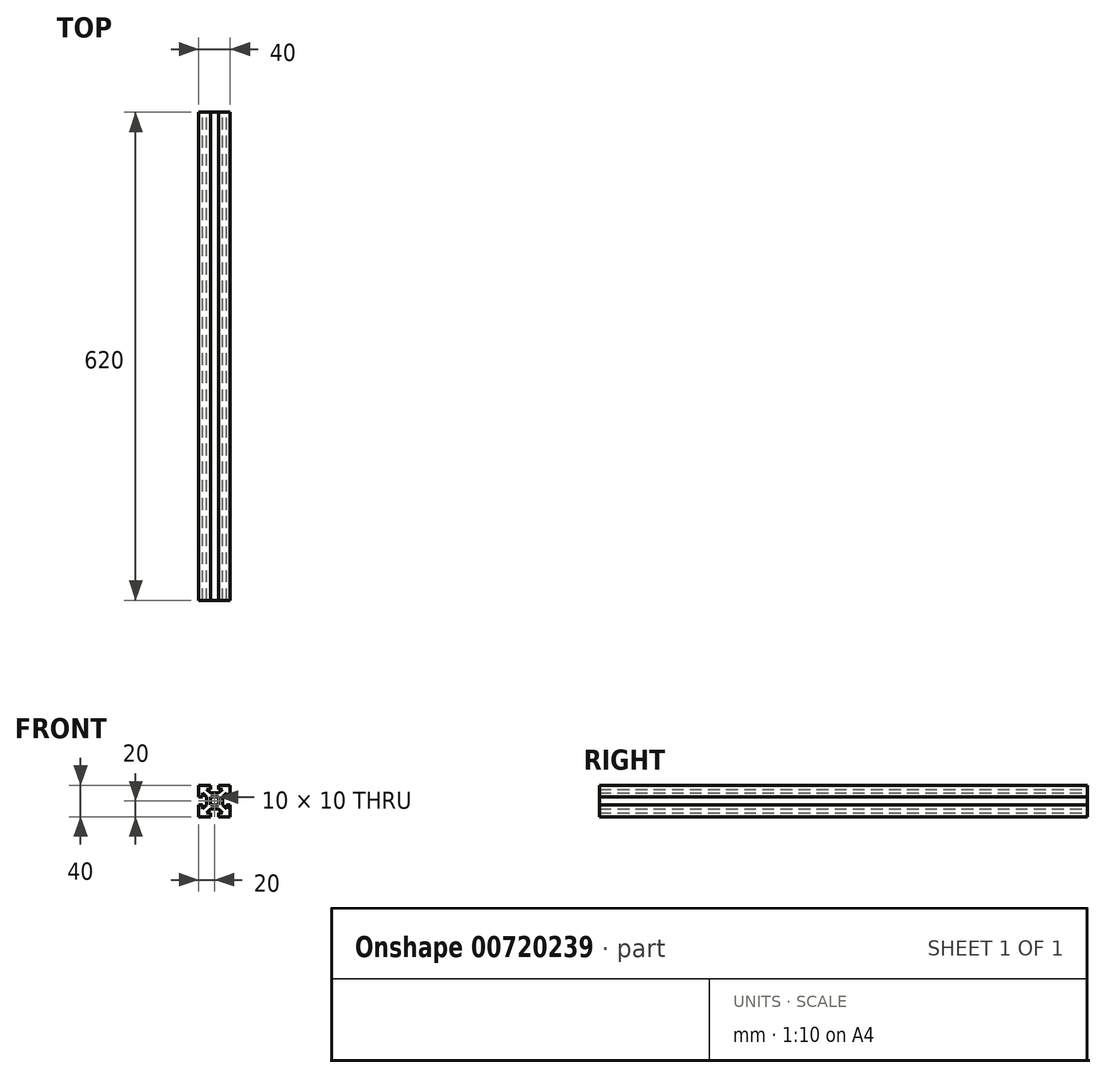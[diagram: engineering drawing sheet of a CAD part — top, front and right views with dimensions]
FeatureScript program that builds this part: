
annotation { "Feature Type Name" : "Feature", "Feature Type Description" : "" }
export const myFeature = defineFeature(function(context is Context, id is Id, definition is map)
    precondition{}
    {
        {
            var Q0;
            Q0=qCreatedBy(makeId("Front.planeOp"),FACE);
            var sketch = newSketch(context, id + "F0", { "sketchPlane" : qUnion([Q0])});
            skLineSegment(sketch, "E0.bottom", {"start": v(20, 20) * mm, "end": v(5, 20) * mm});
            skLineSegment(sketch, "E0.top", {"start": v(20, -20) * mm, "end": v(5, -20) * mm});
            skLineSegment(sketch, "E0.left", {"start": v(20, 20) * mm, "end": v(20, 5) * mm});
            skLineSegment(sketch, "E0.right", {"start": v(-20, 20) * mm, "end": v(-20, 5) * mm});
            skPoint(sketch, "E0.middle", {"position": v(0, 0) * mm});
            skLineSegment(sketch, "E1", {"start": v(0, 20) * mm, "end": v(0, -20) * mm, "construction": true});
            skLineSegment(sketch, "E2", {"start": v(-20, 0) * mm, "end": v(20, 0) * mm, "construction": true});
            skLineSegment(sketch, "E3", {"start": v(-20, 5) * mm, "end": v(-15, 5) * mm});
            skLineSegment(sketch, "E4", {"start": v(-20, -5) * mm, "end": v(-15, -5) * mm});
            skLineSegment(sketch, "E5", {"start": v(-5, 20) * mm, "end": v(-5, 15) * mm});
            skLineSegment(sketch, "E6", {"start": v(5, 20) * mm, "end": v(5, 15) * mm});
            skLineSegment(sketch, "E7", {"start": v(-10, 15) * mm, "end": v(-5, 15) * mm});
            skLineSegment(sketch, "E8", {"start": v(-10, -15) * mm, "end": v(-5, -15) * mm});
            skLineSegment(sketch, "E9", {"start": v(15, 10) * mm, "end": v(15, 5) * mm});
            skLineSegment(sketch, "E10", {"start": v(-15, 10) * mm, "end": v(-10, 5) * mm});
            skLineSegment(sketch, "E11", {"start": v(-10, 15) * mm, "end": v(-5, 10) * mm});
            skLineSegment(sketch, "E12", {"start": v(-15, -10) * mm, "end": v(-10, -5) * mm});
            skLineSegment(sketch, "E13", {"start": v(-10, -15) * mm, "end": v(-5, -10) * mm});
            skLineSegment(sketch, "E14.trimOffspring", {"start": v(20, -5) * mm, "end": v(20, -20) * mm});
            skLineSegment(sketch, "E15.trimOffspring", {"start": v(-20, -5) * mm, "end": v(-20, -20) * mm});
            skLineSegment(sketch, "E16.trimOffspring", {"start": v(-5, -20) * mm, "end": v(-20, -20) * mm});
            skLineSegment(sketch, "E17.trimOffspring", {"start": v(-5, 20) * mm, "end": v(-20, 20) * mm});
            skLineSegment(sketch, "E18.trimOffspring", {"start": v(5, 15) * mm, "end": v(10, 15) * mm});
            skLineSegment(sketch, "E19.trimOffspring", {"start": v(-15, -5) * mm, "end": v(-15, -10) * mm});
            skLineSegment(sketch, "E20.trimOffspring", {"start": v(15, -5) * mm, "end": v(15, -10) * mm});
            skLineSegment(sketch, "E21.trimOffspring", {"start": v(5, -15) * mm, "end": v(10, -15) * mm});
            skLineSegment(sketch, "E22.trimOffspring", {"start": v(-5, 5) * mm, "end": v(-5, -5) * mm});
            skLineSegment(sketch, "E23.trimOffspring", {"start": v(5, 5) * mm, "end": v(5, -5) * mm});
            skLineSegment(sketch, "E24.trimOffspring", {"start": v(15, 5) * mm, "end": v(20, 5) * mm});
            skLineSegment(sketch, "E25.trimOffspring", {"start": v(15, -5) * mm, "end": v(20, -5) * mm});
            skLineSegment(sketch, "E26.trimOffspring", {"start": v(5, -15) * mm, "end": v(5, -20) * mm});
            skLineSegment(sketch, "E27.trimOffspring", {"start": v(-5, -15) * mm, "end": v(-5, -20) * mm});
            skLineSegment(sketch, "E28.trimOffspring", {"start": v(-5, -5) * mm, "end": v(5, -5) * mm});
            skLineSegment(sketch, "E29.trimOffspring", {"start": v(-5, 5) * mm, "end": v(5, 5) * mm});
            skLineSegment(sketch, "E30", {"start": v(10, 5) * mm, "end": v(10, -5) * mm});
            skLineSegment(sketch, "E31", {"start": v(-5, 10) * mm, "end": v(5, 10) * mm});
            skLineSegment(sketch, "E32", {"start": v(-10, 5) * mm, "end": v(-10, -5) * mm});
            skLineSegment(sketch, "E33", {"start": v(-5, -10) * mm, "end": v(5, -10) * mm});
            skLineSegment(sketch, "E34.trimOffspring", {"start": v(-15, 10) * mm, "end": v(-15, 5) * mm});
            skPoint(sketch, "E35.orphan", {"position": v(20, 15) * mm});
            skPoint(sketch, "E36.orphan", {"position": v(20, -15) * mm});
            skPoint(sketch, "E37.orphan", {"position": v(15, -20) * mm});
            skPoint(sketch, "E38.orphan", {"position": v(-15, -20) * mm});
            skLineSegment(sketch, "E39.trimOffspring", {"start": v(-5, 0) * mm, "end": v(0, -5) * mm});
            skLineSegment(sketch, "E40.trimOffspring", {"start": v(-5, 0) * mm, "end": v(0, 5) * mm});
            skLineSegment(sketch, "E41.trimOffspring", {"start": v(0, 5) * mm, "end": v(5, 0) * mm});
            skLineSegment(sketch, "E42.trimOffspring", {"start": v(5, 10) * mm, "end": v(10, 15) * mm});
            skLineSegment(sketch, "E43.trimOffspring", {"start": v(10, 5) * mm, "end": v(15, 10) * mm});
            skLineSegment(sketch, "E44.trimOffspring", {"start": v(10, -5) * mm, "end": v(15, -10) * mm});
            skLineSegment(sketch, "E45.trimOffspring", {"start": v(5, -10) * mm, "end": v(10, -15) * mm});
            skLineSegment(sketch, "E46.trimOffspring", {"start": v(0, -5) * mm, "end": v(5, 0) * mm});
            skSolve(sketch);
        }
        {
            var Q0;
            Q0=makeQuery(id+"F0.imprint","IMPRINT",FACE,{"disambiguationData":[TD([[makeQuery(id+"F0.imprint","IMPRINT",EDGE,{"derivedFrom":sQuery(id+"F0.wireOp",EDGE,"E0.bottom")}),1.0]])]});
            extrude(context, id + "F1", {"entities" : qUnion([Q0]), "depth" : 620 * mm, "offsetDistance" : 25 * mm});
        }
    });
